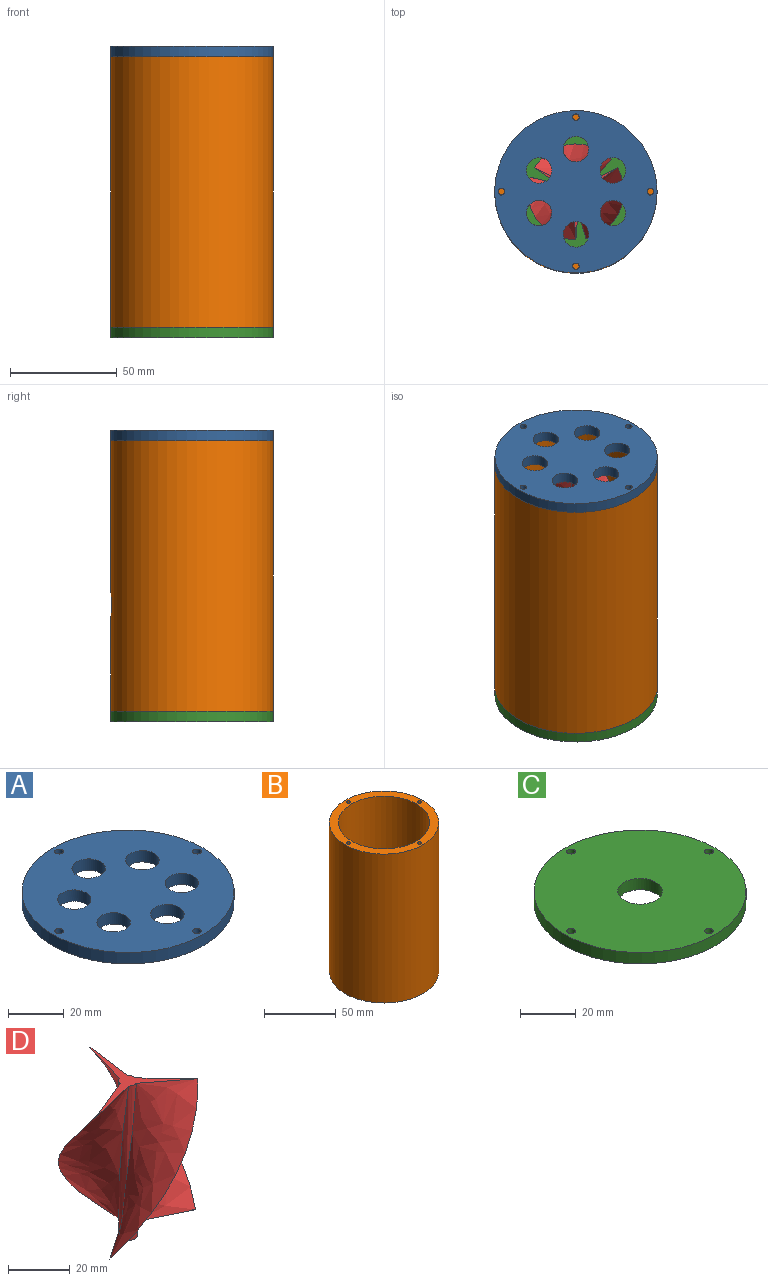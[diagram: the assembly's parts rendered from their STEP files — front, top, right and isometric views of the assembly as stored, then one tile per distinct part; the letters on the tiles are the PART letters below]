
ASSEMBLY  parts=4 mates=3
PART A: 13 faces, bbox 76.2x76.2x5 mm
  f0: cylinder r=38.1mm len=76.2mm, axis (0,0,-1), area 1196.9mm2, adj f1,f2
  f1: plane 76.2x76.2mm, normal (0,0,1), area 3851.6mm2, adj f0,f3,f4,f5,f6,f7,f8,f9
  f2: plane 76.2x76.2mm, normal (0,0,-1), area 3851.6mm2, adj f0,f3,f4,f5,f6,f7,f8,f9
  f3: cylinder r=6mm len=12mm, axis (0,0,-1), area 188.5mm2, adj f1,f2
  f4: cylinder r=6mm len=12mm, axis (0,0,-1), area 188.5mm2, adj f1,f2
  f5: cylinder r=6mm len=12mm, axis (0,0,-1), area 188.5mm2, adj f1,f2
  f6: cylinder r=6mm len=12mm, axis (0,0,-1), area 188.5mm2, adj f1,f2
  f7: cylinder r=6mm len=12mm, axis (0,0,-1), area 188.5mm2, adj f1,f2
  f8: cylinder r=6mm len=12mm, axis (0,0,-1), area 188.5mm2, adj f1,f2
  f9: cylinder r=1.55mm len=5mm, axis (0,0,-1), area 48.7mm2, adj f1,f2
  f10: cylinder r=1.55mm len=5mm, axis (0,0,-1), area 48.7mm2, adj f1,f2
  f11: cylinder r=1.55mm len=5mm, axis (0,0,-1), area 48.7mm2, adj f1,f2
  f12: cylinder r=1.55mm len=5mm, axis (0,0,-1), area 48.7mm2, adj f1,f2
PART B: 21 faces, bbox 76.2x76.2x127 mm
  f0: cylinder r=31.75mm len=127mm, axis (0,0,-1), area 25220.9mm2, adj f2,f3,f4
  f1: cylinder r=38.1mm len=127mm, axis (0,0,-1), area 30288.1mm2, adj f2,f3,f4
  f2: plane 76.2x76.2mm, normal (0,0,1), area 1365.2mm2, adj f0,f1,f5,f7,f9,f11
  f3: plane 76.2x76.2mm, normal (0,0,-1), area 1365.2mm2, adj f0,f1,f13,f15,f17,f19
  f4: cylinder r=6mm len=12mm, axis (0,-1,0), area 241.2mm2, adj f0,f1
  f5: cylinder r=1.5mm len=10mm, axis (0,0,1), area 94.2mm2, adj f2,f6
  f6: plane 3x3mm, normal (0,0,1), area 7.1mm2, adj f5
  f7: cylinder r=1.5mm len=10mm, axis (0,0,1), area 94.2mm2, adj f2,f8
  f8: plane 3x3mm, normal (0,0,1), area 7.1mm2, adj f7
  f9: cylinder r=1.5mm len=10mm, axis (0,0,1), area 94.2mm2, adj f2,f10
  f10: plane 3x3mm, normal (0,0,1), area 7.1mm2, adj f9
  f11: cylinder r=1.5mm len=10mm, axis (0,0,1), area 94.2mm2, adj f2,f12
  f12: plane 3x3mm, normal (0,0,1), area 7.1mm2, adj f11
  f13: cylinder r=1.5mm len=20mm, axis (0,0,-1), area 188.5mm2, adj f3,f14
  f14: plane 3x3mm, normal (0,0,-1), area 7.1mm2, adj f13
  f15: cylinder r=1.5mm len=20mm, axis (0,0,-1), area 188.5mm2, adj f3,f16
  f16: plane 3x3mm, normal (0,0,-1), area 7.1mm2, adj f15
  f17: cylinder r=1.5mm len=20mm, axis (0,0,-1), area 188.5mm2, adj f3,f18
  f18: plane 3x3mm, normal (0,0,-1), area 7.1mm2, adj f17
  f19: cylinder r=1.5mm len=20mm, axis (0,0,-1), area 188.5mm2, adj f3,f20
  f20: plane 3x3mm, normal (0,0,-1), area 7.1mm2, adj f19
PART C: 8 faces, bbox 76.2x76.2x5 mm
  f0: cylinder r=8mm len=16mm, axis (0,0,-1), area 251.3mm2, adj f2,f3
  f1: cylinder r=38.1mm len=76.2mm, axis (0,0,-1), area 1196.9mm2, adj f2,f3
  f2: plane 76.2x76.2mm, normal (0,0,1), area 4329.1mm2, adj f0,f1,f4,f5,f6,f7
  f3: plane 76.2x76.2mm, normal (0,0,-1), area 4329.1mm2, adj f0,f1,f4,f5,f6,f7
  f4: cylinder r=1.55mm len=5mm, axis (0,0,-1), area 48.7mm2, adj f2,f3
  f5: cylinder r=1.55mm len=5mm, axis (0,0,-1), area 48.7mm2, adj f2,f3
  f6: cylinder r=1.55mm len=5mm, axis (0,0,-1), area 48.7mm2, adj f2,f3
  f7: cylinder r=1.55mm len=5mm, axis (0,0,-1), area 48.7mm2, adj f2,f3
PART D: 13 faces, bbox 45.1x45.3x61 mm
  f0: plane 19.94x3mm, normal (0,0,-1), area 29.1mm2, adj f6,f8,f9
  f1: plane 18.02x11.27mm, normal (0,0,-1), area 29.1mm2, adj f6,f10,f11
  f2: plane 18.02x11.27mm, normal (0,0,-1), area 29.1mm2, adj f4,f5,f6
  f3: plane 38.19x37.13mm, normal (0,0,1), area 115.6mm2, adj f4,f5,f6,f7,f8,f9,f10,f11
  f4: bspline ~55x33.32mm, area 1213.1mm2, adj f2,f3,f5,f6
  f5: bspline ~55x33.32mm, area 1213.1mm2, adj f2,f3,f4,f6,f7
  f6: cylinder r=3mm len=61mm, axis (0,0,-1), area 600.8mm2, adj f0,f1,f2,f3,f4,f5,f7,f8
  f7: cylinder r=3mm len=24.45mm, axis (0,0,-1), area 30.7mm2, adj f3,f5,f6
  f8: bspline ~55x29.51mm, area 1213.1mm2, adj f0,f3,f6,f9
  f9: bspline ~55x29.51mm, area 1213.1mm2, adj f0,f3,f6,f8
  f10: bspline ~55x36.27mm, area 1213.1mm2, adj f1,f3,f6,f11
  f11: bspline ~55x36.27mm, area 1213.1mm2, adj f1,f3,f6,f10
  f12: plane 6x6mm, normal (0,0,-1), area 28.3mm2, adj f6
PLACE A rot(axis=(1,0,0),180deg) t=(-116.32,-54.12,-21.69)mm
PLACE B t=(-116.32,-54.12,-153.69)mm
PLACE C rot(axis=(1,0,0),180deg) t=(-116.32,-54.12,-153.69)mm
PLACE D rot(axis=(1,0,0),180deg) t=(-116.32,-54.12,-32.69)mm
MATE fastened A.f11 <-> B.f9  axis (0,0,1) through (-151.32,-54.12,-26.69)mm
MATE fastened D.f6 <-> A.f0  axis (0,0,1) through (-116.32,-54.12,-26.69)mm
MATE fastened C.f6 <-> B.f13  axis (0,0,1) through (-151.32,-54.12,-153.69)mm
